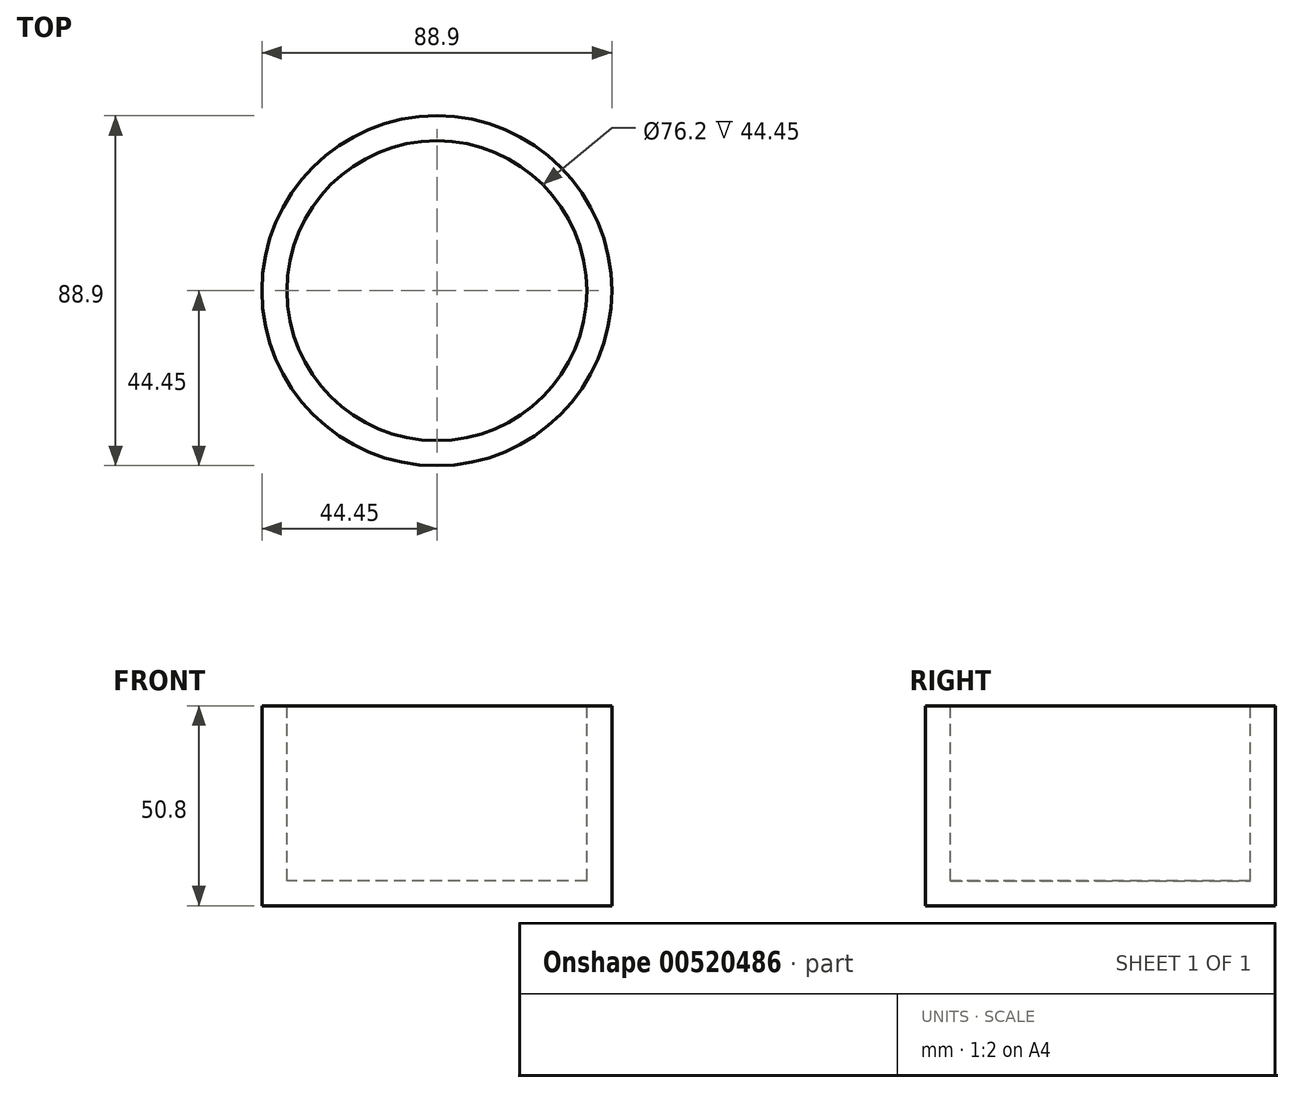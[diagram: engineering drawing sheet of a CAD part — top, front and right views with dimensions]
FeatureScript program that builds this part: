
annotation { "Feature Type Name" : "Feature", "Feature Type Description" : "" }
export const myFeature = defineFeature(function(context is Context, id is Id, definition is map)
    precondition{}
    {
        {
            var Q0;
            Q0=qCreatedBy(makeId("Top.planeOp"),FACE);
            var sketch = newSketch(context, id + "F0", { "sketchPlane" : qUnion([Q0])});
            skCircle(sketch, "E0", {"center": v(0, 0) * mm, "radius": 44.45 * mm});
            skSolve(sketch);
        }
        {
            var Q0;
            Q0=makeQuery(id+"F0.imprint","IMPRINT",FACE,{"disambiguationData":[TD([[makeQuery(id+"F0.imprint","IMPRINT",EDGE,{"derivedFrom":sQuery(id+"F0.wireOp",EDGE,"E0")}),1.0]])]});
            extrude(context, id + "F1", {"entities" : qUnion([Q0]), "depth" : 50.8 * mm, "offsetDistance" : 25.4 * mm});
        }
        {
            var Q0;
            Q0=makeQuery(id+"F1.opExtrude","CAP_FACE",FACE,{"disambiguationData":[OSD([sQuery(id+"F0.wireOp",EDGE,"E0")])],"isStart":false});
            var sketch = newSketch(context, id + "F2", { "sketchPlane" : qUnion([Q0])});
            skCircle(sketch, "E1", {"center": v(0, 0) * mm, "radius": 38.1 * mm});
            skSolve(sketch);
        }
        {
            var Q0;
            Q0=makeQuery(id+"F2.imprint","IMPRINT",FACE,{"disambiguationData":[TD([[makeQuery(id+"F2.imprint","IMPRINT",EDGE,{"derivedFrom":sQuery(id+"F2.wireOp",EDGE,"E1")}),1.0]])]});
            extrude(context, id + "F3", {"entities" : qUnion([Q0]), "operationType" : NewBodyOperationType.REMOVE, "oppositeDirection" : true, "depth" : 44.45 * mm, "offsetDistance" : 25.4 * mm});
        }
    });
